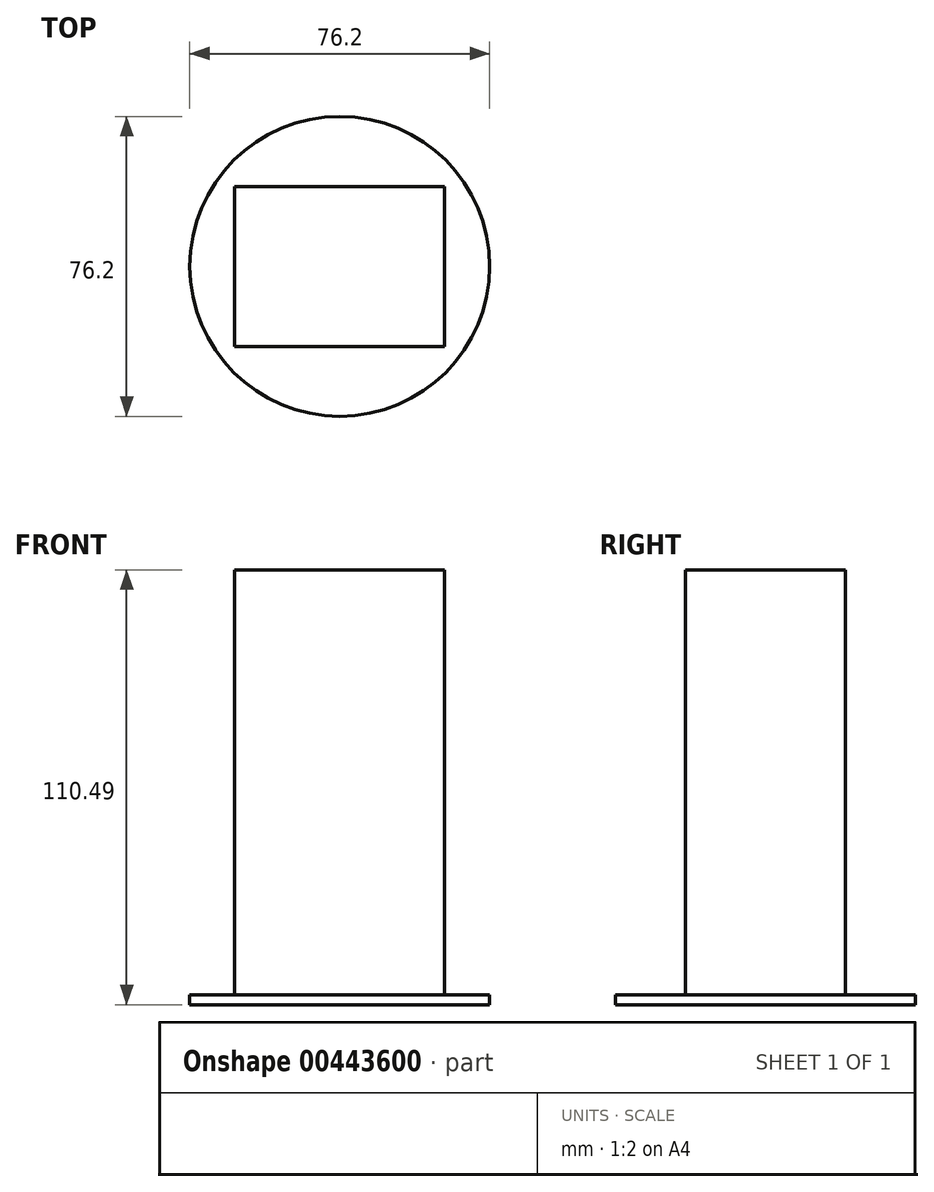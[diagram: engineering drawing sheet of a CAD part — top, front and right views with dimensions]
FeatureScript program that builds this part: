
annotation { "Feature Type Name" : "Feature", "Feature Type Description" : "" }
export const myFeature = defineFeature(function(context is Context, id is Id, definition is map)
    precondition{}
    {
        {
            var Q0;
            Q0=qCreatedBy(makeId("Top.planeOp"),FACE);
            var sketch = newSketch(context, id + "F0", { "sketchPlane" : qUnion([Q0])});
            skLineSegment(sketch, "E0.bottom", {"start": v(26.67, 20.32) * mm, "end": v(-26.67, 20.32) * mm});
            skLineSegment(sketch, "E0.top", {"start": v(26.67, -20.32) * mm, "end": v(-26.67, -20.32) * mm});
            skLineSegment(sketch, "E0.left", {"start": v(26.67, 20.32) * mm, "end": v(26.67, -20.32) * mm});
            skLineSegment(sketch, "E0.right", {"start": v(-26.67, 20.32) * mm, "end": v(-26.67, -20.32) * mm});
            skPoint(sketch, "E0.middle", {"position": v(0, 0) * mm});
            skSolve(sketch);
        }
        {
            var Q0;
            Q0=makeQuery(id+"F0.imprint","IMPRINT",FACE,{"disambiguationData":[TD([[makeQuery(id+"F0.imprint","IMPRINT",EDGE,{"derivedFrom":sQuery(id+"F0.wireOp",EDGE,"E0.bottom")}),1.0]])]});
            extrude(context, id + "F1", {"entities" : qUnion([Q0]), "depth" : 107.95 * mm});
        }
        {
            var Q0;
            Q0=makeQuery(id+"F1.opExtrude","CAP_FACE",FACE,{"disambiguationData":[OSD([sQuery(id+"F0.wireOp",EDGE,"E0.bottom"),sQuery(id+"F0.wireOp",EDGE,"E0.top"),sQuery(id+"F0.wireOp",EDGE,"E0.left"),sQuery(id+"F0.wireOp",EDGE,"E0.right")])],"isStart":true});
            var sketch = newSketch(context, id + "F2", { "sketchPlane" : qUnion([Q0])});
            skCircle(sketch, "E1", {"center": v(0, 0) * mm, "radius": 38.1 * mm});
            skSolve(sketch);
        }
        {
            var Q0;
            Q0 = qSketchRegion(id + "F2", true);
            extrude(context, id + "F3", {"entities" : qUnion([Q0]), "operationType" : NewBodyOperationType.ADD, "depth" : 2.54 * mm});
        }
    });
